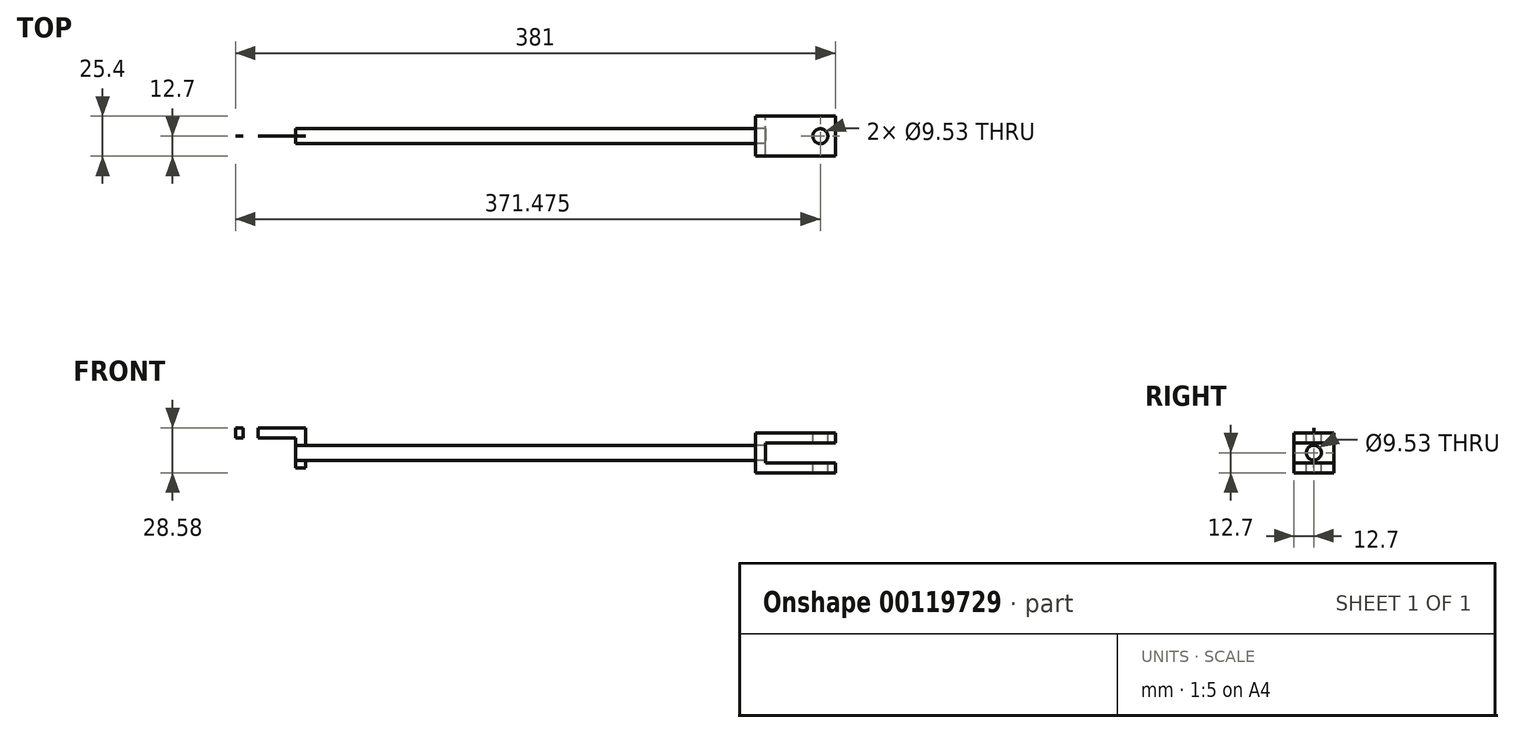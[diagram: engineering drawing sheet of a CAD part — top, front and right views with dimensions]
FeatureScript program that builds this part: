
annotation { "Feature Type Name" : "Feature", "Feature Type Description" : "" }
export const myFeature = defineFeature(function(context is Context, id is Id, definition is map)
    precondition{}
    {
        {
            var Q0;
            Q0=qCreatedBy(makeId("Right.planeOp"),FACE);
            var sketch = newSketch(context, id + "F0", { "sketchPlane" : qUnion([Q0])});
            skCircle(sketch, "E0", {"center": v(0, 0) * mm, "radius": 4.76 * mm});
            skSolve(sketch);
        }
        {
            var Q0;
            Q0=qSketchRegion(id+"F0",true);
            extrude(context, id + "F1", {"entities" : qUnion([Q0]), "depth" : 298.45 * mm});
        }
        {
            var Q0;
            Q0=qCreatedBy(makeId("Front.planeOp"),FACE);
            var sketch = newSketch(context, id + "F2", { "sketchPlane" : qUnion([Q0])});
            skLineSegment(sketch, "E1", {"start": v(0, 9.52) * mm, "end": v(0, -9.52) * mm});
            skLineSegment(sketch, "E2", {"start": v(0, -9.52) * mm, "end": v(6.35, -9.52) * mm});
            skLineSegment(sketch, "E3", {"start": v(6.35, -9.52) * mm, "end": v(6.35, 15.88) * mm});
            skLineSegment(sketch, "E4", {"start": v(6.35, 15.88) * mm, "end": v(-38.1, 15.88) * mm});
            skLineSegment(sketch, "E5", {"start": v(-38.1, 15.88) * mm, "end": v(-38.1, 9.52) * mm});
            skLineSegment(sketch, "E6", {"start": v(-38.1, 9.52) * mm, "end": v(0, 9.52) * mm});
            skSolve(sketch);
        }
        {
            var Q0;
            Q0=qSketchRegion(id+"F2",true);
            extrude(context, id + "F3", {"entities" : qUnion([Q0]), "endBound" : BoundingType.SYMMETRIC, "depth" : 3 / 101.6 * mm});
        }
        {
            var Q0;
            Q0=makeQuery(id+"F1.opExtrude","SWEPT_BODY",BODY,{"disambiguationData":[OSD([sQuery(id+"F0.wireOp",EDGE,"E0")])]});
            var Q1;
            Q1=makeQuery(id+"F3.opExtrude","SWEPT_BODY",BODY,{"disambiguationData":[OSD([sQuery(id+"F2.wireOp",EDGE,"E1"),sQuery(id+"F2.wireOp",EDGE,"E2"),sQuery(id+"F2.wireOp",EDGE,"E3"),sQuery(id+"F2.wireOp",EDGE,"E4"),sQuery(id+"F2.wireOp",EDGE,"E5"),sQuery(id+"F2.wireOp",EDGE,"E6")])]});
            booleanBodies(context, id + "F4", {"operationType" : BooleanOperationType.SUBTRACTION, "tools" : qUnion([Q0]), "targets" : qUnion([Q1]), "keepTools" : true});
        }
        {
            var Q0;
            Q0=makeQuery(id+"F3.opExtrude","SWEPT_FACE",FACE,{"disambiguationData":[OSD([sQuery(id+"F2.wireOp",EDGE,"E4")])]});
            var sketch = newSketch(context, id + "F5", { "sketchPlane" : qUnion([Q0])});
            skCircle(sketch, "E7", {"center": v(-28.58, 0) * mm, "radius": 4.76 * mm});
            skPoint(sketch, "E7.centerSnap0", {"position": v(-38.1, 0) * mm});
            skSolve(sketch);
        }
        {
            var Q0;
            Q0=qSketchRegion(id+"F5",true);
            extrude(context, id + "F6", {"entities" : qUnion([Q0]), "operationType" : NewBodyOperationType.REMOVE, "endBound" : BoundingType.THROUGH_ALL, "oppositeDirection" : true, "depth" : 25 * mm});
        }
        {
            var Q0;
            Q0=qCreatedBy(makeId("Front.planeOp"),FACE);
            var sketch = newSketch(context, id + "F7", { "sketchPlane" : qUnion([Q0])});
            skLineSegment(sketch, "E8", {"start": v(292.1, 12.7) * mm, "end": v(292.1, -12.7) * mm});
            skLineSegment(sketch, "E9", {"start": v(292.1, -12.7) * mm, "end": v(342.9, -12.7) * mm});
            skLineSegment(sketch, "E10", {"start": v(342.9, -12.7) * mm, "end": v(342.9, -6.35) * mm});
            skLineSegment(sketch, "E11", {"start": v(342.9, -6.35) * mm, "end": v(298.45, -6.35) * mm});
            skLineSegment(sketch, "E12", {"start": v(298.45, -6.35) * mm, "end": v(298.45, 6.35) * mm});
            skLineSegment(sketch, "E13", {"start": v(298.45, 6.35) * mm, "end": v(342.9, 6.35) * mm});
            skLineSegment(sketch, "E14", {"start": v(342.9, 6.35) * mm, "end": v(342.9, 12.7) * mm});
            skLineSegment(sketch, "E15", {"start": v(342.9, 12.7) * mm, "end": v(292.1, 12.7) * mm});
            skPoint(sketch, "E16", {"position": v(292.1, 0) * mm});
            skSolve(sketch);
        }
        {
            var Q0;
            Q0=qSketchRegion(id+"F7",true);
            extrude(context, id + "F8", {"entities" : qUnion([Q0]), "endBound" : BoundingType.SYMMETRIC, "depth" : 25.4 * mm});
        }
        {
            var Q0;
            Q0=makeQuery(id+"F1.opExtrude","SWEPT_BODY",BODY,{"disambiguationData":[OSD([sQuery(id+"F0.wireOp",EDGE,"E0")])]});
            var Q1;
            Q1=makeQuery(id+"F8.opExtrude","SWEPT_BODY",BODY,{"disambiguationData":[OSD([sQuery(id+"F7.wireOp",EDGE,"E8"),sQuery(id+"F7.wireOp",EDGE,"E9"),sQuery(id+"F7.wireOp",EDGE,"E10"),sQuery(id+"F7.wireOp",EDGE,"E11"),sQuery(id+"F7.wireOp",EDGE,"E12"),sQuery(id+"F7.wireOp",EDGE,"E13"),sQuery(id+"F7.wireOp",EDGE,"E14"),sQuery(id+"F7.wireOp",EDGE,"E15")])]});
            booleanBodies(context, id + "F9", {"operationType" : BooleanOperationType.SUBTRACTION, "tools" : qUnion([Q0]), "targets" : qUnion([Q1]), "keepTools" : true});
        }
        {
            var Q0;
            Q0=makeQuery(id+"F8.opExtrude","SWEPT_FACE",FACE,{"disambiguationData":[OSD([sQuery(id+"F7.wireOp",EDGE,"E15")])]});
            var sketch = newSketch(context, id + "F10", { "sketchPlane" : qUnion([Q0])});
            skCircle(sketch, "E17", {"center": v(333.38, 0) * mm, "radius": 4.76 * mm});
            skPoint(sketch, "E17.centerSnap0", {"position": v(342.9, 0) * mm});
            skSolve(sketch);
        }
        {
            var Q0;
            Q0=qSketchRegion(id+"F10",true);
            extrude(context, id + "F11", {"entities" : qUnion([Q0]), "operationType" : NewBodyOperationType.REMOVE, "endBound" : BoundingType.THROUGH_ALL, "oppositeDirection" : true, "depth" : 25 * mm});
        }
    });
